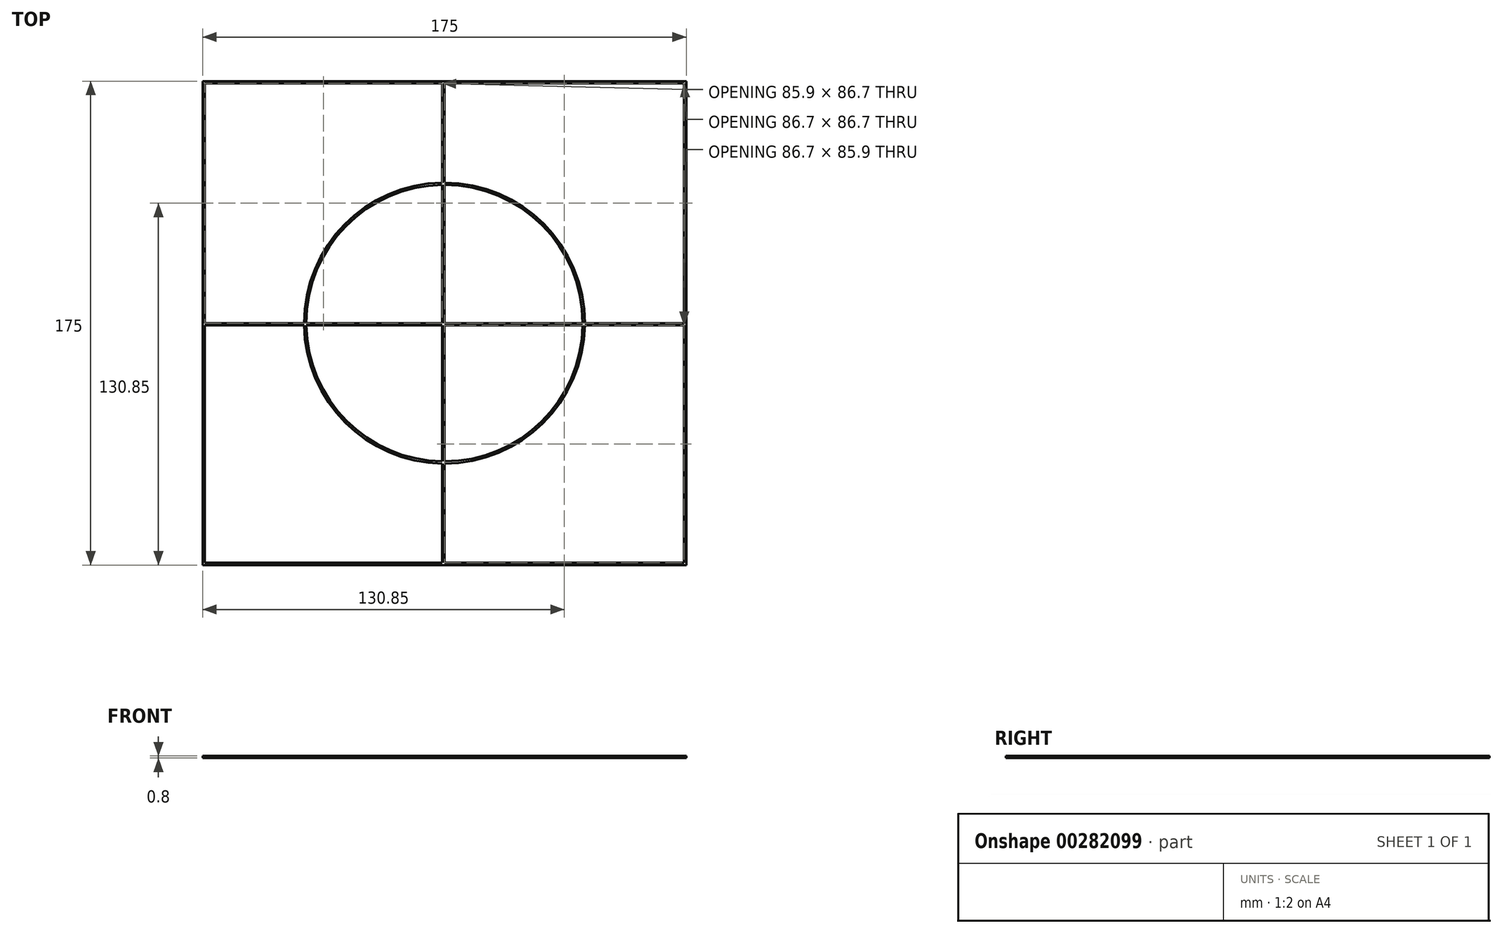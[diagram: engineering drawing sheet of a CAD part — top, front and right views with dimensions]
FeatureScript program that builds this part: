
annotation { "Feature Type Name" : "Feature", "Feature Type Description" : "" }
export const myFeature = defineFeature(function(context is Context, id is Id, definition is map)
    precondition{}
    {
        {
            var Q0;
            Q0=qCreatedBy(makeId("Top.planeOp"),FACE);
            var sketch = newSketch(context, id + "F0", { "sketchPlane" : qUnion([Q0])});
            skLineSegment(sketch, "E0.bottom", {"start": v(87.5, 87.5) * mm, "end": v(-87.5, 87.5) * mm});
            skLineSegment(sketch, "E0.top", {"start": v(87.5, -87.5) * mm, "end": v(-87.5, -87.5) * mm});
            skLineSegment(sketch, "E0.left", {"start": v(87.5, 87.5) * mm, "end": v(87.5, -87.5) * mm});
            skLineSegment(sketch, "E0.right", {"start": v(-87.5, 87.5) * mm, "end": v(-87.5, -87.5) * mm});
            skPoint(sketch, "E0.middle", {"position": v(0, 0) * mm});
            skLineSegment(sketch, "E1.0", {"start": v(86.7, 86.7) * mm, "end": v(0, 86.7) * mm});
            skLineSegment(sketch, "E1.1", {"start": v(86.7, 86.7) * mm, "end": v(86.7, 0) * mm});
            skLineSegment(sketch, "E1.2", {"start": v(86.7, -86.7) * mm, "end": v(0, -86.7) * mm});
            skLineSegment(sketch, "E1.3", {"start": v(-86.7, 86.7) * mm, "end": v(-86.7, -86.7) * mm});
            skLineSegment(sketch, "E2.0.left", {"start": v(0, 86.7) * mm, "end": v(0, 0) * mm});
            skLineSegment(sketch, "E2.0.right", {"start": v(-0.8, 86.7) * mm, "end": v(-0.8, 0) * mm});
            skLineSegment(sketch, "E3.0.left", {"start": v(-86.7, 0) * mm, "end": v(-0.8, 0) * mm});
            skLineSegment(sketch, "E3.0.right", {"start": v(-86.7, -0.8) * mm, "end": v(-0.8, -0.8) * mm});
            skLineSegment(sketch, "E4.trimOffspring", {"start": v(0, -0.8) * mm, "end": v(0, -86.7) * mm});
            skLineSegment(sketch, "E5.trimOffspring", {"start": v(0, 0) * mm, "end": v(86.7, 0) * mm});
            skLineSegment(sketch, "E6.trimOffspring", {"start": v(-0.8, -0.8) * mm, "end": v(-0.8, -86.7) * mm});
            skLineSegment(sketch, "E7.trimOffspring", {"start": v(0, -0.8) * mm, "end": v(86.7, -0.8) * mm});
            skLineSegment(sketch, "E8.trimOffspring", {"start": v(-0.8, -86.7) * mm, "end": v(-86.7, -86.7) * mm});
            skPoint(sketch, "E9.trimOffspring.end.orphan", {"position": v(0, -87.5) * mm});
            skPoint(sketch, "E10.trimOffspring.end.orphan", {"position": v(87.5, 0) * mm});
            skLineSegment(sketch, "E11.trimOffspring", {"start": v(86.7, -0.8) * mm, "end": v(86.7, -86.7) * mm});
            skPoint(sketch, "E12.start.orphan", {"position": v(0, 87.5) * mm});
            skLineSegment(sketch, "E13.trimOffspring", {"start": v(-0.8, 86.7) * mm, "end": v(-86.7, 86.7) * mm});
            skPoint(sketch, "E14.start.orphan", {"position": v(-87.5, 0) * mm});
            skCircle(sketch, "E15", {"center": v(0, 0) * mm, "radius": 50 * mm});
            skCircle(sketch, "E16", {"center": v(0, 0) * mm, "radius": 50.8 * mm});
            skLineSegment(sketch, "E17", {"start": v(-0.8, 0) * mm, "end": v(0, -0.8) * mm});
            skLineSegment(sketch, "E18", {"start": v(0, 87.5) * mm, "end": v(0, -87.5) * mm, "construction": true});
            skSolve(sketch);
        }
        {
            var Q0;
            Q0=makeQuery(id+"F0.imprint","IMPRINT",FACE,{"disambiguationData":[TD([[makeQuery(id+"F0.imprint","IMPRINT",EDGE,{"derivedFrom":sQuery(id+"F0.wireOp",EDGE,"E0.bottom")}),1.0]])]});
            var Q1;
            {var subQ0=sQuery(id+"F0.wireOp",EDGE,"E16");var subQ1=sQuery(id+"F0.wireOp",EDGE,"E2.0.right");var subQ2=makeQuery(id+"F0.imprint","INTERSECT",VERTEX,{"derivedFrom":[subQ1,subQ0]});Q1=makeQuery(id+"F0.imprint","IMPRINT",FACE,{"disambiguationData":[TD([[makeQuery(id+"F0.imprint","IMPRINT",EDGE,{"disambiguationData":[TD([[subQ2,-1.0]])],"derivedFrom":subQ1}),-1.0]])]});}
            var Q2;
            {var subQ0=sQuery(id+"F0.wireOp",EDGE,"E16");var subQ1=sQuery(id+"F0.wireOp",EDGE,"E3.0.left");var subQ2=makeQuery(id+"F0.imprint","INTERSECT",VERTEX,{"derivedFrom":[subQ1,subQ0]});Q2=makeQuery(id+"F0.imprint","IMPRINT",FACE,{"disambiguationData":[TD([[makeQuery(id+"F0.imprint","IMPRINT",EDGE,{"disambiguationData":[TD([[subQ2,-1.0]])],"derivedFrom":subQ1}),-1.0]])]});}
            var Q3;
            {var subQ0=sQuery(id+"F0.wireOp",EDGE,"E16");var subQ1=sQuery(id+"F0.wireOp",EDGE,"E3.0.right");var subQ2=makeQuery(id+"F0.imprint","INTERSECT",VERTEX,{"derivedFrom":[subQ1,subQ0]});Q3=makeQuery(id+"F0.imprint","IMPRINT",FACE,{"disambiguationData":[TD([[makeQuery(id+"F0.imprint","IMPRINT",EDGE,{"disambiguationData":[TD([[subQ2,-1.0]])],"derivedFrom":subQ1}),-1.0]])]});}
            var Q4;
            {var subQ1=sQuery(id+"F0.wireOp",EDGE,"E2.0.left");var subQ15=sQuery(id+"F0.wireOp",EDGE,"E5.trimOffspring");var subQ16=makeQuery(id+"F0.imprint","INTERSECT",VERTEX,{"derivedFrom":[subQ1,subQ15]});Q4=makeQuery(id+"F0.imprint","IMPRINT",FACE,{"disambiguationData":[TD([[makeQuery(id+"F0.imprint","IMPRINT",EDGE,{"disambiguationData":[TD([[subQ16,1.0]])],"derivedFrom":subQ1}),-1.0]])]});}
            var Q5;
            {var subQ0=sQuery(id+"F0.wireOp",EDGE,"E3.0.left");var subQ1=sQuery(id+"F0.wireOp",EDGE,"E1.3");var subQ2=makeQuery(id+"F0.imprint","INTERSECT",VERTEX,{"derivedFrom":[subQ1,subQ0]});Q5=makeQuery(id+"F0.imprint","IMPRINT",FACE,{"disambiguationData":[TD([[makeQuery(id+"F0.imprint","IMPRINT",EDGE,{"disambiguationData":[TD([[subQ2,-1.0]])],"derivedFrom":subQ1}),1.0]])]});}
            var Q6;
            {var subQ0=sQuery(id+"F0.wireOp",EDGE,"E16");var subQ1=sQuery(id+"F0.wireOp",EDGE,"E2.0.left");var subQ2=makeQuery(id+"F0.imprint","INTERSECT",VERTEX,{"derivedFrom":[subQ1,subQ0]});Q6=makeQuery(id+"F0.imprint","IMPRINT",FACE,{"disambiguationData":[TD([[makeQuery(id+"F0.imprint","IMPRINT",EDGE,{"disambiguationData":[TD([[subQ2,-1.0]])],"derivedFrom":subQ1}),1.0]])]});}
            var Q7;
            {var subQ0=sQuery(id+"F0.wireOp",EDGE,"E15");var subQ1=sQuery(id+"F0.wireOp",EDGE,"E5.trimOffspring");var subQ2=makeQuery(id+"F0.imprint","INTERSECT",VERTEX,{"derivedFrom":[subQ1,subQ0]});Q7=makeQuery(id+"F0.imprint","IMPRINT",FACE,{"disambiguationData":[TD([[makeQuery(id+"F0.imprint","IMPRINT",EDGE,{"disambiguationData":[TD([[subQ2,-1.0]])],"derivedFrom":subQ1}),-1.0]])]});}
            var Q8;
            {var subQ0=sQuery(id+"F0.wireOp",EDGE,"E15");var subQ1=sQuery(id+"F0.wireOp",EDGE,"E4.trimOffspring");var subQ2=makeQuery(id+"F0.imprint","INTERSECT",VERTEX,{"derivedFrom":[subQ1,subQ0]});Q8=makeQuery(id+"F0.imprint","IMPRINT",FACE,{"disambiguationData":[TD([[makeQuery(id+"F0.imprint","IMPRINT",EDGE,{"disambiguationData":[TD([[subQ2,-1.0]])],"derivedFrom":subQ1}),1.0]])]});}
            var Q9;
            {var subQ0=sQuery(id+"F0.wireOp",EDGE,"E15");var subQ1=sQuery(id+"F0.wireOp",EDGE,"E4.trimOffspring");var subQ2=makeQuery(id+"F0.imprint","INTERSECT",VERTEX,{"derivedFrom":[subQ1,subQ0]});Q9=makeQuery(id+"F0.imprint","IMPRINT",FACE,{"disambiguationData":[TD([[makeQuery(id+"F0.imprint","IMPRINT",EDGE,{"disambiguationData":[TD([[subQ2,-1.0]])],"derivedFrom":subQ1}),-1.0]])]});}
            var Q10;
            {var subQ0=sQuery(id+"F0.wireOp",EDGE,"E16");var subQ1=sQuery(id+"F0.wireOp",EDGE,"E2.0.left");var subQ2=makeQuery(id+"F0.imprint","INTERSECT",VERTEX,{"derivedFrom":[subQ1,subQ0]});Q10=makeQuery(id+"F0.imprint","IMPRINT",FACE,{"disambiguationData":[TD([[makeQuery(id+"F0.imprint","IMPRINT",EDGE,{"disambiguationData":[TD([[subQ2,-1.0]])],"derivedFrom":subQ1}),-1.0]])]});}
            var Q11;
            {var subQ0=sQuery(id+"F0.wireOp",EDGE,"E17");Q11=makeQuery(id+"F0.imprint","IMPRINT",FACE,{"disambiguationData":[TD([[makeQuery(id+"F0.imprint","IMPRINT",EDGE,{"derivedFrom":subQ0}),-1.0]])]});}
            extrude(context, id + "F1", {"entities" : qUnion([Q0, Q1, Q2, Q3, Q4, Q5, Q6, Q7, Q8, Q9, Q10, Q11]), "depth" : .8 * mm, "offsetDistance" : 25 * mm});
        }
    });
